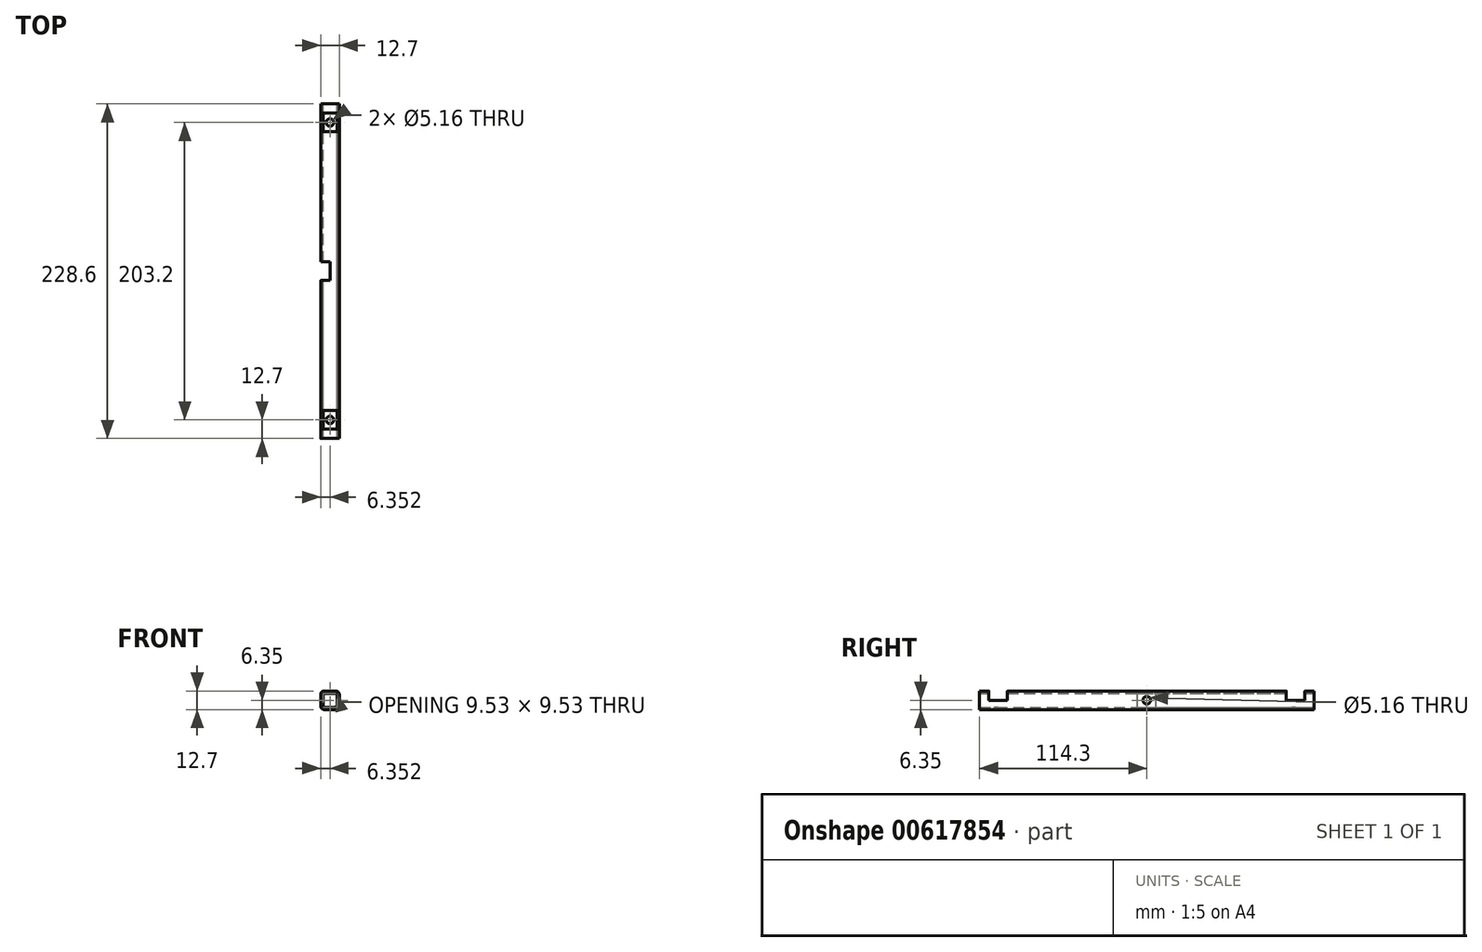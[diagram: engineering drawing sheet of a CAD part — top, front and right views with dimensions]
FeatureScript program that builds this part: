
annotation { "Feature Type Name" : "Feature", "Feature Type Description" : "" }
export const myFeature = defineFeature(function(context is Context, id is Id, definition is map)
    precondition{}
    {
        {
            var Q0;
            Q0=qCreatedBy(makeId("Front.planeOp"),FACE);
            var sketch = newSketch(context, id + "F0", { "sketchPlane" : qUnion([Q0])});
            skLineSegment(sketch, "E0.bottom", {"start": v(7.7, 0) * mm, "end": v(-0.25, 0) * mm});
            skLineSegment(sketch, "E0.top", {"start": v(7.7, -12.7) * mm, "end": v(-0.25, -12.7) * mm});
            skLineSegment(sketch, "E0.left", {"start": v(10.07, -2.38) * mm, "end": v(10.07, -10.32) * mm});
            skLineSegment(sketch, "E0.right", {"start": v(-2.63, -2.38) * mm, "end": v(-2.63, -10.32) * mm});
            skPoint(sketch, "E0.middle", {"position": v(3.72, -6.35) * mm});
            skPoint(sketch, "E1.visualSharp", {"position": v(-2.63, 0) * mm});
            skArc(sketch, "E1.filletArc", {"start": v(-0.25, 0) * mm, "mid": v(-1.93, -0.7) * mm, "end": v(-2.63, -2.38) * mm});
            skPoint(sketch, "E2.visualSharp", {"position": v(-2.63, -12.7) * mm});
            skArc(sketch, "E2.filletArc", {"start": v(-2.63, -10.32) * mm, "mid": v(-1.93, -12) * mm, "end": v(-0.25, -12.7) * mm});
            skPoint(sketch, "E3.visualSharp", {"position": v(10.07, -12.7) * mm});
            skArc(sketch, "E3.filletArc", {"start": v(7.7, -12.7) * mm, "mid": v(9.37, -12) * mm, "end": v(10.07, -10.32) * mm});
            skPoint(sketch, "E4.visualSharp", {"position": v(10.07, 0) * mm});
            skArc(sketch, "E4.filletArc", {"start": v(10.07, -2.38) * mm, "mid": v(9.37, -0.7) * mm, "end": v(7.7, 0) * mm});
            skLineSegment(sketch, "E5.bottom", {"start": v(6.9, -1.59) * mm, "end": v(0.55, -1.59) * mm});
            skLineSegment(sketch, "E5.top", {"start": v(6.9, -11.11) * mm, "end": v(0.55, -11.11) * mm});
            skLineSegment(sketch, "E5.left", {"start": v(8.48, -3.17) * mm, "end": v(8.48, -9.53) * mm});
            skLineSegment(sketch, "E5.right", {"start": v(-1.04, -3.18) * mm, "end": v(-1.04, -9.53) * mm});
            skPoint(sketch, "E6.visualSharp", {"position": v(-1.04, -1.59) * mm});
            skArc(sketch, "E6.filletArc", {"start": v(0.55, -1.59) * mm, "mid": v(-0.58, -2.05) * mm, "end": v(-1.04, -3.18) * mm});
            skPoint(sketch, "E7.visualSharp", {"position": v(8.48, -1.59) * mm});
            skArc(sketch, "E7.filletArc", {"start": v(8.48, -3.17) * mm, "mid": v(8.02, -2.05) * mm, "end": v(6.9, -1.59) * mm});
            skPoint(sketch, "E8.visualSharp", {"position": v(8.48, -11.11) * mm});
            skArc(sketch, "E8.filletArc", {"start": v(6.9, -11.11) * mm, "mid": v(8.02, -10.65) * mm, "end": v(8.48, -9.53) * mm});
            skPoint(sketch, "E9.visualSharp", {"position": v(-1.04, -11.11) * mm});
            skArc(sketch, "E9.filletArc", {"start": v(-1.04, -9.53) * mm, "mid": v(-0.58, -10.65) * mm, "end": v(0.55, -11.11) * mm});
            skSolve(sketch);
        }
        {
            var Q0;
            Q0=qSketchRegion(id+"F0",true);
            extrude(context, id + "F1", {"entities" : qUnion([Q0]), "depth" : 228.6 * mm, "offsetDistance" : 25.4 * mm});
        }
        {
            var Q0;
            Q0=qCreatedBy(makeId("Right.planeOp"),FACE);
            var sketch = newSketch(context, id + "F2", { "sketchPlane" : qUnion([Q0])});
            skLineSegment(sketch, "E10.bottom", {"start": v(-222.25, 0) * mm, "end": v(-209.55, 0) * mm});
            skLineSegment(sketch, "E10.top", {"start": v(-222.25, -6.35) * mm, "end": v(-209.55, -6.35) * mm});
            skLineSegment(sketch, "E10.left", {"start": v(-222.25, 0) * mm, "end": v(-222.25, -6.35) * mm});
            skLineSegment(sketch, "E10.right", {"start": v(-209.55, 0) * mm, "end": v(-209.55, -6.35) * mm});
            skLineSegment(sketch, "E11.bottom", {"start": v(-6.35, 0) * mm, "end": v(-19.05, 0) * mm});
            skLineSegment(sketch, "E11.top", {"start": v(-6.35, -6.35) * mm, "end": v(-19.05, -6.35) * mm});
            skLineSegment(sketch, "E11.left", {"start": v(-6.35, 0) * mm, "end": v(-6.35, -6.35) * mm});
            skLineSegment(sketch, "E11.right", {"start": v(-19.05, 0) * mm, "end": v(-19.05, -6.35) * mm});
            skSolve(sketch);
        }
        {
            var Q0;
            Q0 = qSketchRegion(id + "F2", true);
            extrude(context, id + "F3", {"entities" : qUnion([Q0]), "operationType" : NewBodyOperationType.REMOVE, "depth" : 11.94 * mm, "offsetDistance" : 25.4 * mm, "hasSecondDirection" : true, "secondDirectionOppositeDirection" : true, "secondDirectionDepth" : 25.4 * mm});
        }
        {
            var Q0;
            Q0=qCreatedBy(makeId("Top.planeOp"),FACE);
            var sketch = newSketch(context, id + "F4", { "sketchPlane" : qUnion([Q0])});
            skLineSegment(sketch, "E12.bottom", {"start": v(3.72, -107.95) * mm, "end": v(-2.63, -107.95) * mm});
            skLineSegment(sketch, "E12.top", {"start": v(3.72, -120.65) * mm, "end": v(-2.63, -120.65) * mm});
            skLineSegment(sketch, "E12.left", {"start": v(3.72, -107.95) * mm, "end": v(3.72, -120.65) * mm});
            skLineSegment(sketch, "E12.right", {"start": v(-2.63, -107.95) * mm, "end": v(-2.63, -120.65) * mm});
            skSolve(sketch);
        }
        {
            var Q0;
            Q0 = qSketchRegion(id + "F4", true);
            extrude(context, id + "F5", {"entities" : qUnion([Q0]), "operationType" : NewBodyOperationType.REMOVE, "oppositeDirection" : true, "depth" : 12.7 * mm, "offsetDistance" : 25.4 * mm});
        }
        {
            var Q0;
            Q0=qCreatedBy(makeId("Top.planeOp"),FACE);
            var sketch = newSketch(context, id + "F6", { "sketchPlane" : qUnion([Q0])});
            skCircle(sketch, "E13", {"center": v(3.72, -12.7) * mm, "radius": 2.58 * mm});
            skCircle(sketch, "E14", {"center": v(3.72, -215.9) * mm, "radius": 2.58 * mm});
            skSolve(sketch);
        }
        {
            var Q0;
            Q0 = qSketchRegion(id + "F6", true);
            extrude(context, id + "F7", {"entities" : qUnion([Q0]), "operationType" : NewBodyOperationType.REMOVE, "oppositeDirection" : true, "depth" : 12.7 * mm, "offsetDistance" : 25.4 * mm});
        }
        {
            var Q0;
            Q0=qCreatedBy(makeId("Right.planeOp"),FACE);
            var sketch = newSketch(context, id + "F8", { "sketchPlane" : qUnion([Q0])});
            skCircle(sketch, "E15", {"center": v(-114.3, -6.35) * mm, "radius": 2.58 * mm});
            skSolve(sketch);
        }
        {
            var Q0;
            Q0 = qSketchRegion(id + "F8", true);
            extrude(context, id + "F9", {"entities" : qUnion([Q0]), "operationType" : NewBodyOperationType.REMOVE, "depth" : 12.7 * mm, "offsetDistance" : 25.4 * mm});
        }
    });
